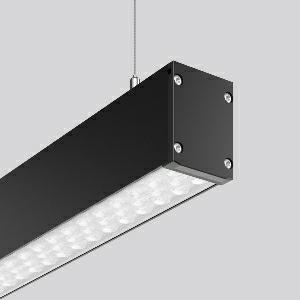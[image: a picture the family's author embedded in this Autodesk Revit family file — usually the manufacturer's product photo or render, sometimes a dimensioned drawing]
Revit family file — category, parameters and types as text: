
# Revit family: linedo_single_ip54_312565_003_1_76_98f6
name_source: partatom
category: Lighting Fixtures
units: mm (PartAtom-declared; Revit-internal decimal feet)

## family parameters
Cut with Voids When Loaded = No
Host = Face
Light Source = No
Part Type = Normal
Room Calculation Point = No
Round Connector Dimension = Use Diameter
Shared = No

## types (1)
- LINEDO single IP54 (1 x LED Modul 840, 4850 lm, 4000)
    Apparent Load = 31 VA
    CIE Flux Codes = 86 96 99 100 100
    Color Rendering = 80
    Color Temperature = 4000
    Default Elevation = 1800 mm
    Description = Series: LINEDO single IP54
Stylish pendant luminaire. Housing: extruded aluminium profile, powder-coated. Plastic end caps, black. High-efficiency LED units with optimum light control thanks to clear plastic (PC) lens optics. 2-point steel cable suspension freely positionable and infinitely height-adjustable. With power cord (2.5 m). Please order canopy separately if required. Perfect for office areas (RUG < 19) and environments with computer screens in accordance with EN 12464-1. Luminaire with limited surface temperature in accordance with EN 60598-2-24 for use in environments in which a deposit of conductive dust on the luminaire can be expected. 
Colour: jet black (RAL 9005)
Length: 1710 mm
Width: 58 mm
Height: 76 mm
Suspension length: 100-1500 mm
Lamp: LED
Socket: without socket
Colour temperature: 4000K
Colour rendering index (CRI): 80
System power: 31 W
Rated luminous flux: 4850 lm
Beam angle Down: 59°
Luminous efficiency: 156 lm/W
Control gear: Converter, dimmable, DALI
Protection class: I
Type of protection: IP 54
    Height = 76 mm
    Lamp = 1 x LED Modul 840
    Lamp Light Flux = 4850 lm
    Lamp count = 1
    Length = 1710 mm
    Lifetime = 50000 h
    Luminous efficacy = 156 lm/W
    Manufacturer = RZB
    ModVariant = No
    Model = 312565.003.1.76
    Mounting Place = Ceiling
    Mounting Type = Surface mounted, Pendant
    Number of Poles = 1
    OnlyDefault = Yes
    Power Factor = 1
    Product Name = LINEDO single IP54
    Product group = Pendant luminaires
    ProductGroupID = 902
    Protection Class = Protection class I
    Protection Degree = IP 54
    RLX_Detail_Level = 1
    RLX_Emergency_Light_Flux = 0 lm
    RLX_Emergency_Type = 0
    RLX_Emergency_Type_DB = No
    RlxData = <blob elided: 35945 chars, md5=6c8e65ea>
    Socket = socket
    Standby Power = 0 W
    System Light Flux = 4850 lm
    System Power = 31 W
    Type Comments = ALEA SPOT
    Type Image = 312565.003.jpg
    URL = http://relux.com
    VarID = ---
    Voltage = 230 V
    Voltage Range = 220-240 V
    Weight = 0.00 kg
    Width = 58 mm

## geometry (parser evidence)
native form markers: Blend x4, Sweep x11
no freeform markers — native parametric forms only
